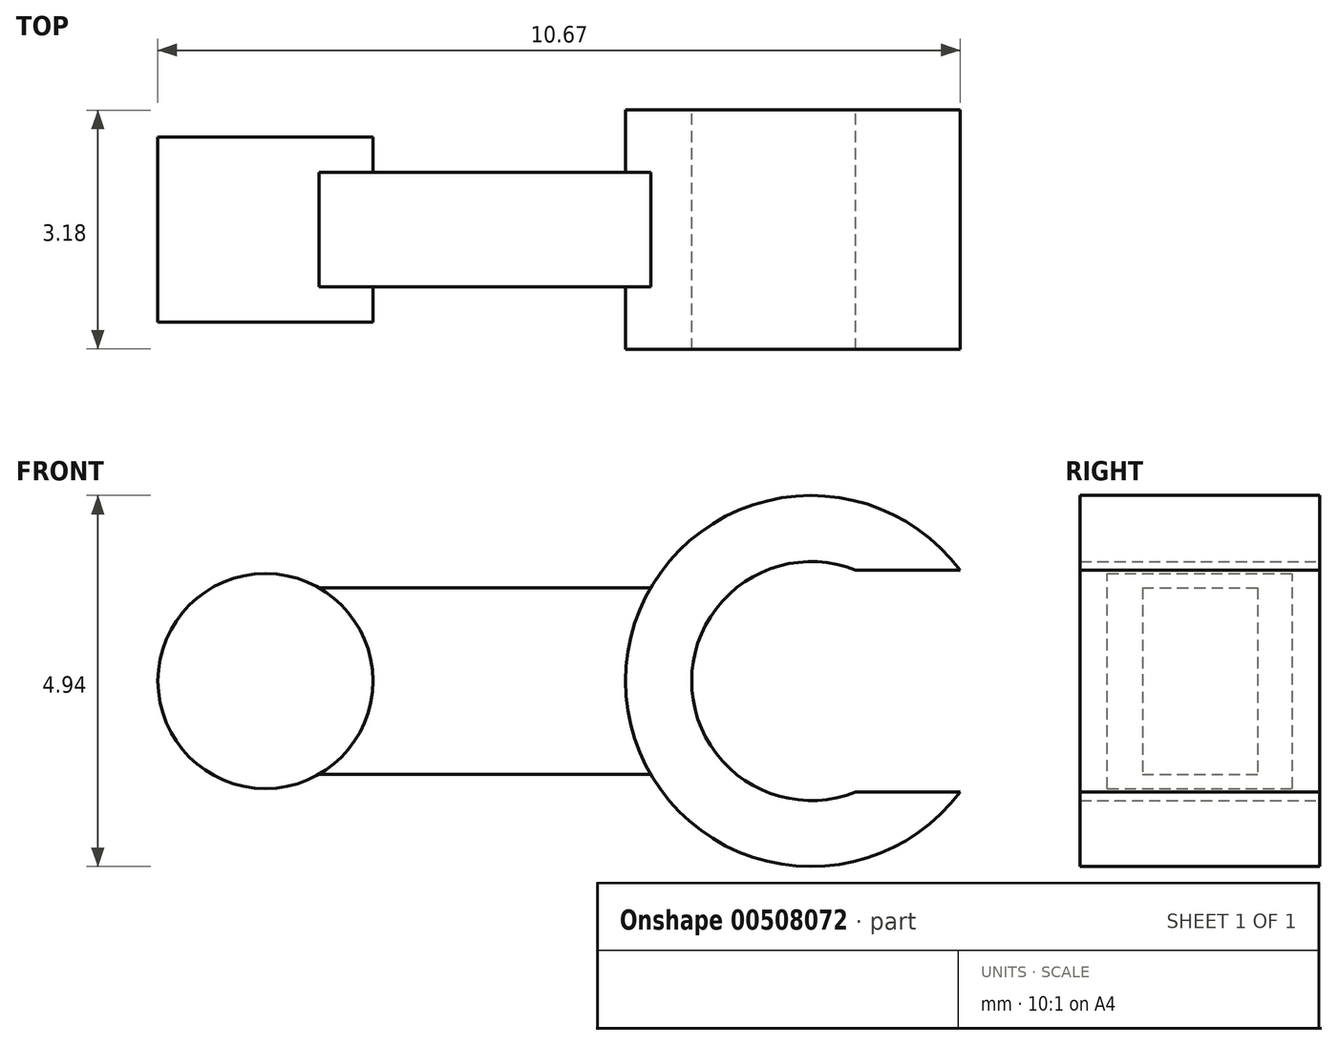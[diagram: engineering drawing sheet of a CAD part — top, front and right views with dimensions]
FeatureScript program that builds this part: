
annotation { "Feature Type Name" : "Feature", "Feature Type Description" : "" }
export const myFeature = defineFeature(function(context is Context, id is Id, definition is map)
    precondition{}
    {
        {
            var Q0;
            Q0=qCreatedBy(makeId("Front.planeOp"),FACE);
            var sketch = newSketch(context, id + "F0", { "sketchPlane" : qUnion([Q0])});
            skCircle(sketch, "E0", {"center": v(0, 0) * mm, "radius": 2.47 * mm});
            skCircle(sketch, "E1", {"center": v(0, 0) * mm, "radius": 1.59 * mm});
            skLineSegment(sketch, "E2", {"start": v(1.7, 0) * mm, "end": v(1.7, 1.48) * mm});
            skLineSegment(sketch, "E3", {"start": v(1.7, 1.48) * mm, "end": v(1.98, 1.48) * mm});
            skLineSegment(sketch, "E4", {"start": v(1.7, 1.48) * mm, "end": v(0.6, 1.47) * mm});
            skLineSegment(sketch, "E5", {"start": v(1.7, 0) * mm, "end": v(1.7, -1.48) * mm});
            skLineSegment(sketch, "E6", {"start": v(1.7, -1.48) * mm, "end": v(0.6, -1.48) * mm});
            skLineSegment(sketch, "E7", {"start": v(1.7, -1.48) * mm, "end": v(1.98, -1.48) * mm});
            skLineSegment(sketch, "E8", {"start": v(-2.47, 0) * mm, "end": v(-5.83, 0) * mm});
            skLineSegment(sketch, "E9", {"start": v(-5.83, 0) * mm, "end": v(-5.83, 1.24) * mm});
            skLineSegment(sketch, "E10", {"start": v(-5.83, 0) * mm, "end": v(-5.83, -1.24) * mm});
            skLineSegment(sketch, "E11", {"start": v(-5.83, 1.24) * mm, "end": v(-2.14, 1.24) * mm});
            skLineSegment(sketch, "E12", {"start": v(-5.83, -1.24) * mm, "end": v(-2.14, -1.24) * mm});
            skCircle(sketch, "E13", {"center": v(-7.26, 0) * mm, "radius": 1.43 * mm});
            skPoint(sketch, "E13.second.point", {"position": v(-8.7, 0) * mm});
            skPoint(sketch, "E13.third.point", {"position": v(-8.1, 1.15) * mm});
            skLineSegment(sketch, "E14", {"start": v(-5.83, 1.24) * mm, "end": v(-6.55, 1.24) * mm});
            skLineSegment(sketch, "E15", {"start": v(-5.83, -1.24) * mm, "end": v(-6.55, -1.24) * mm});
            skSolve(sketch);
        }
        {
            var Q0;
            {var subQ0=sQuery(id+"F0.wireOp",EDGE,"E13");var subQ2=makeQuery(id+"F0.imprint","INTERSECT",VERTEX,{"derivedFrom":[subQ0,sQuery(id+"F0.wireOp",EDGE,"E14")]});Q0=makeQuery(id+"F0.imprint","IMPRINT",FACE,{"disambiguationData":[TD([[makeQuery(id+"F0.imprint","IMPRINT",EDGE,{"disambiguationData":[TD([[subQ2,-1.0]])],"derivedFrom":subQ0}),1.0]])]});}
            extrude(context, id + "F1", {"entities" : qUnion([Q0]), "depth" : 1.23 * mm, "offsetDistance" : 25 * mm});
        }
        {
            var Q0;
            {var subQ0=sQuery(id+"F0.wireOp",EDGE,"E9");Q0=makeQuery(id+"F0.imprint","IMPRINT",FACE,{"disambiguationData":[TD([[makeQuery(id+"F0.imprint","IMPRINT",EDGE,{"derivedFrom":subQ0}),1.0]])]});}
            var Q1;
            {var subQ0=sQuery(id+"F0.wireOp",EDGE,"E10");Q1=makeQuery(id+"F0.imprint","IMPRINT",FACE,{"disambiguationData":[TD([[makeQuery(id+"F0.imprint","IMPRINT",EDGE,{"derivedFrom":subQ0}),-1.0]])]});}
            var Q2;
            {var subQ0=sQuery(id+"F0.wireOp",EDGE,"E8");Q2=makeQuery(id+"F0.imprint","IMPRINT",FACE,{"disambiguationData":[TD([[makeQuery(id+"F0.imprint","IMPRINT",EDGE,{"derivedFrom":subQ0}),-1.0]])]});}
            var Q3;
            {var subQ0=sQuery(id+"F0.wireOp",EDGE,"E8");Q3=makeQuery(id+"F0.imprint","IMPRINT",FACE,{"disambiguationData":[TD([[makeQuery(id+"F0.imprint","IMPRINT",EDGE,{"derivedFrom":subQ0}),1.0]])]});}
            extrude(context, id + "F2", {"entities" : qUnion([Q0, Q1, Q2, Q3]), "operationType" : NewBodyOperationType.ADD, "depth" : 0.77 * mm, "offsetDistance" : 25 * mm});
        }
        {
            var Q0;
            {var subQ5=sQuery(id+"F0.wireOp",EDGE,"E3");Q0=makeQuery(id+"F0.imprint","IMPRINT",FACE,{"disambiguationData":[TD([[makeQuery(id+"F0.imprint","IMPRINT",EDGE,{"derivedFrom":subQ5}),1.0]])]});}
            extrude(context, id + "F3", {"entities" : qUnion([Q0]), "operationType" : NewBodyOperationType.ADD, "depth" : 1.6 * mm, "offsetDistance" : 25 * mm});
        }
        {
            var Q0;
            {var subQ5=sQuery(id+"F0.wireOp",EDGE,"E3");Q0=makeQuery(id+"F0.imprint","IMPRINT",FACE,{"disambiguationData":[TD([[makeQuery(id+"F0.imprint","IMPRINT",EDGE,{"derivedFrom":subQ5}),1.0]])]});}
            extrude(context, id + "F4", {"entities" : qUnion([Q0]), "operationType" : NewBodyOperationType.ADD, "oppositeDirection" : true, "depth" : 1.6 * mm, "offsetDistance" : 25 * mm});
        }
        {
            var Q0;
            {var subQ0=sQuery(id+"F0.wireOp",EDGE,"E10");Q0=makeQuery(id+"F0.imprint","IMPRINT",FACE,{"disambiguationData":[TD([[makeQuery(id+"F0.imprint","IMPRINT",EDGE,{"derivedFrom":subQ0}),-1.0]])]});}
            var Q1;
            {var subQ0=sQuery(id+"F0.wireOp",EDGE,"E9");Q1=makeQuery(id+"F0.imprint","IMPRINT",FACE,{"disambiguationData":[TD([[makeQuery(id+"F0.imprint","IMPRINT",EDGE,{"derivedFrom":subQ0}),1.0]])]});}
            var Q2;
            {var subQ0=sQuery(id+"F0.wireOp",EDGE,"E8");Q2=makeQuery(id+"F0.imprint","IMPRINT",FACE,{"disambiguationData":[TD([[makeQuery(id+"F0.imprint","IMPRINT",EDGE,{"derivedFrom":subQ0}),-1.0]])]});}
            var Q3;
            {var subQ0=sQuery(id+"F0.wireOp",EDGE,"E8");Q3=makeQuery(id+"F0.imprint","IMPRINT",FACE,{"disambiguationData":[TD([[makeQuery(id+"F0.imprint","IMPRINT",EDGE,{"derivedFrom":subQ0}),1.0]])]});}
            extrude(context, id + "F5", {"entities" : qUnion([Q0, Q1, Q2, Q3]), "operationType" : NewBodyOperationType.ADD, "oppositeDirection" : true, "depth" : 0.77 * mm, "offsetDistance" : 25 * mm});
        }
        {
            var Q0;
            {var subQ0=sQuery(id+"F0.wireOp",EDGE,"E13");var subQ2=makeQuery(id+"F0.imprint","INTERSECT",VERTEX,{"derivedFrom":[subQ0,sQuery(id+"F0.wireOp",EDGE,"E14")]});Q0=makeQuery(id+"F0.imprint","IMPRINT",FACE,{"disambiguationData":[TD([[makeQuery(id+"F0.imprint","IMPRINT",EDGE,{"disambiguationData":[TD([[subQ2,-1.0]])],"derivedFrom":subQ0}),1.0]])]});}
            extrude(context, id + "F6", {"entities" : qUnion([Q0]), "operationType" : NewBodyOperationType.ADD, "oppositeDirection" : true, "depth" : 1.23 * mm, "offsetDistance" : 25 * mm});
        }
    });
